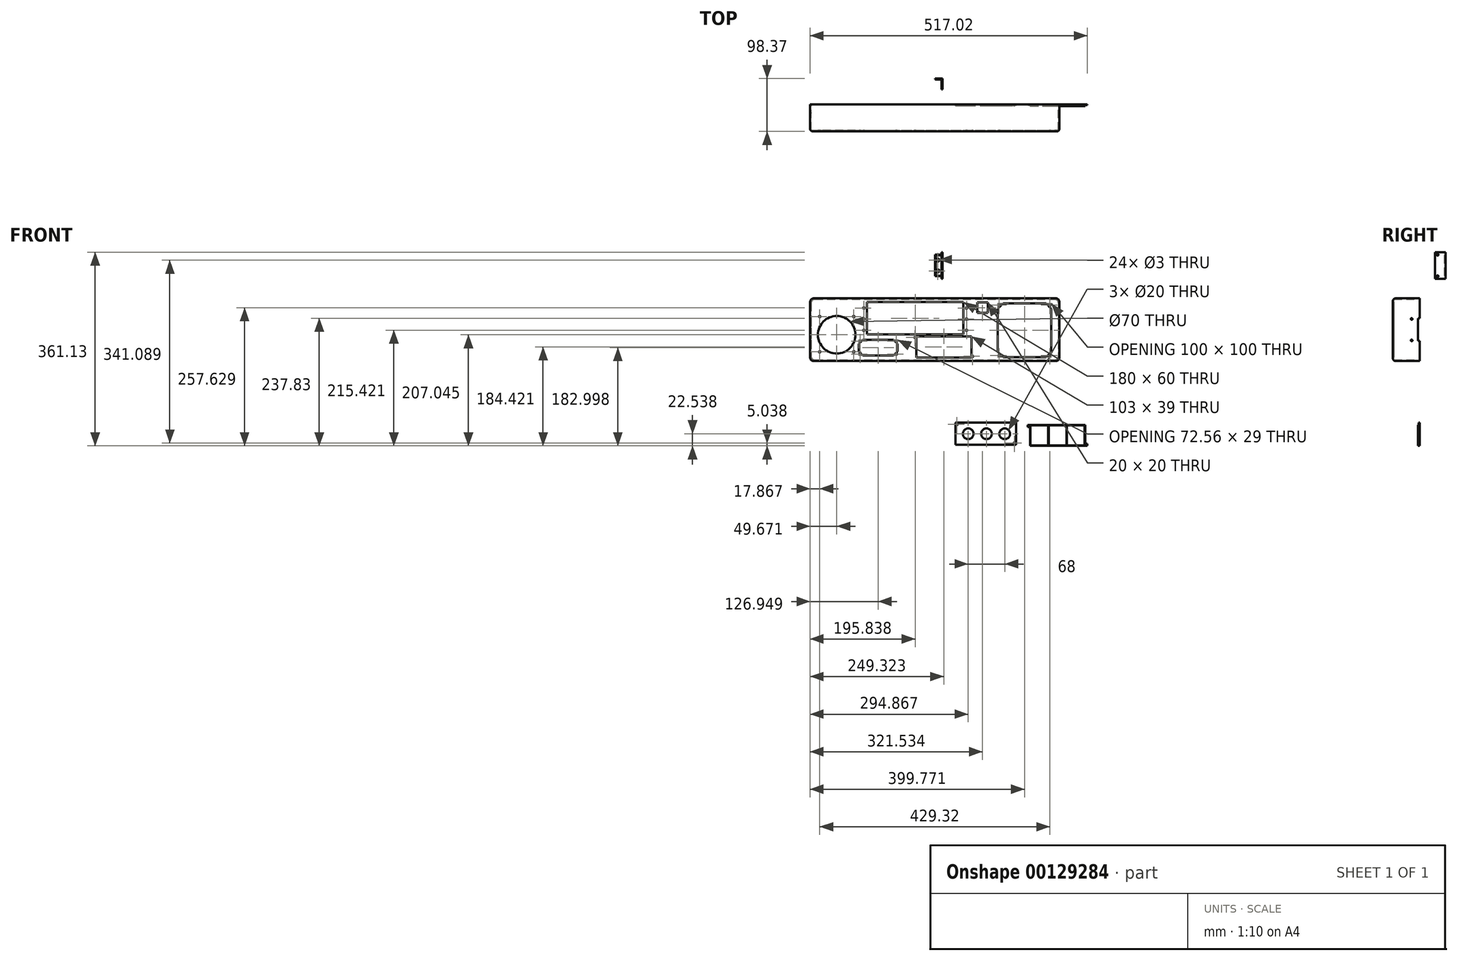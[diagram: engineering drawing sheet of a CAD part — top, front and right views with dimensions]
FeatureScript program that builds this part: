
annotation { "Feature Type Name" : "Feature", "Feature Type Description" : "" }
export const myFeature = defineFeature(function(context is Context, id is Id, definition is map)
    precondition{}
    {
        {
            var Q0;
            Q0=qCreatedBy(makeId("Front.planeOp"),FACE);
            var sketch = newSketch(context, id + "F0", { "sketchPlane" : qUnion([Q0])});
            skLineSegment(sketch, "E0.bottom", {"start": v(-245.15, 85.69) * mm, "end": v(219.85, 85.69) * mm});
            skLineSegment(sketch, "E0.top", {"start": v(-245.15, -31.31) * mm, "end": v(219.85, -31.31) * mm});
            skLineSegment(sketch, "E0.left", {"start": v(-245.15, 85.69) * mm, "end": v(-245.15, -31.31) * mm});
            skLineSegment(sketch, "E0.right", {"start": v(219.85, 85.69) * mm, "end": v(219.85, -31.31) * mm});
            skSolve(sketch);
        }
        {
            var Q0;
            Q0=qSketchRegion(id+"F0",true);
            var Q1;
            Q1=makeQuery(id+"F0.imprint","IMPRINT",FACE,{"disambiguationData":[TD([[makeQuery(id+"F0.imprint","IMPRINT",EDGE,{"derivedFrom":sQuery(id+"F0.wireOp",EDGE,"E0.bottom")}),-1.0]])]});
            extrude(context, id + "F1", {"entities" : qUnion([Q0, Q1]), "depth" : 50 * mm});
        }
        {
            var Q0;
            Q0=makeQuery(id+"F1.opExtrude","CAP_FACE",FACE,{"disambiguationData":[OSD([sQuery(id+"F0.wireOp",EDGE,"E0.bottom"),sQuery(id+"F0.wireOp",EDGE,"E0.top"),sQuery(id+"F0.wireOp",EDGE,"E0.left"),sQuery(id+"F0.wireOp",EDGE,"E0.right")])],"isStart":true});
            shell(context, id + "F2", {"entities" : qUnion([Q0]), "thickness" : 2 * mm});
        }
        {
            var Q0;
            Q0=makeQuery(id+"F1.opExtrude","CAP_FACE",FACE,{"disambiguationData":[OSD([sQuery(id+"F0.wireOp",EDGE,"E0.bottom"),sQuery(id+"F0.wireOp",EDGE,"E0.top"),sQuery(id+"F0.wireOp",EDGE,"E0.left"),sQuery(id+"F0.wireOp",EDGE,"E0.right")])],"isStart":false});
            var sketch = newSketch(context, id + "F3", { "sketchPlane" : qUnion([Q0])});
            skLineSegment(sketch, "E1.bottom", {"start": v(-139.31, 78.52) * mm, "end": v(40.69, 78.52) * mm});
            skLineSegment(sketch, "E1.top", {"start": v(-139.31, 18.52) * mm, "end": v(40.69, 18.52) * mm});
            skLineSegment(sketch, "E1.left", {"start": v(-139.31, 78.52) * mm, "end": v(-139.31, 18.52) * mm});
            skLineSegment(sketch, "E1.right", {"start": v(40.69, 78.52) * mm, "end": v(40.69, 18.52) * mm});
            skLineSegment(sketch, "E2.bottom", {"start": v(66.38, 78.32) * mm, "end": v(86.38, 78.32) * mm});
            skLineSegment(sketch, "E2.top", {"start": v(66.38, 58.32) * mm, "end": v(86.38, 58.32) * mm});
            skLineSegment(sketch, "E2.left", {"start": v(66.38, 78.32) * mm, "end": v(66.38, 58.32) * mm});
            skLineSegment(sketch, "E2.right", {"start": v(86.38, 78.32) * mm, "end": v(86.38, 58.32) * mm});
            skLineSegment(sketch, "E3.bottom", {"start": v(114.52, 76.11) * mm, "end": v(194.72, 76.11) * mm});
            skLineSegment(sketch, "E3.top", {"start": v(114.52, -23.89) * mm, "end": v(194.72, -23.89) * mm});
            skLineSegment(sketch, "E3.left", {"start": v(104.62, 66.21) * mm, "end": v(104.62, -13.99) * mm});
            skLineSegment(sketch, "E3.right", {"start": v(204.62, 66.21) * mm, "end": v(204.62, -13.99) * mm});
            skLineSegment(sketch, "E4.bottom", {"start": v(-128.05, -55.46) * mm, "end": v(-35.05, -55.46) * mm, "construction": true});
            skLineSegment(sketch, "E4.top", {"start": v(-128.05, -91.46) * mm, "end": v(-35.05, -91.46) * mm, "construction": true});
            skLineSegment(sketch, "E4.left", {"start": v(-128.05, -55.46) * mm, "end": v(-128.05, -91.46) * mm, "construction": true});
            skLineSegment(sketch, "E4.right", {"start": v(-35.05, -55.46) * mm, "end": v(-35.05, -91.46) * mm, "construction": true});
            skCircle(sketch, "E5", {"center": v(46.59, 67.55) * mm, "radius": 1.5 * mm});
            skCircle(sketch, "E6", {"center": v(46.59, 47.16) * mm, "radius": 1.5 * mm});
            skCircle(sketch, "E7", {"center": v(46.59, 26.05) * mm, "radius": 1.5 * mm});
            skLineSegment(sketch, "E8.bottom", {"start": v(-233.81, -59.67) * mm, "end": v(-156.81, -59.67) * mm, "construction": true});
            skLineSegment(sketch, "E8.top", {"start": v(-233.81, -136.67) * mm, "end": v(-156.81, -136.67) * mm, "construction": true});
            skLineSegment(sketch, "E8.left", {"start": v(-233.81, -59.67) * mm, "end": v(-233.81, -136.67) * mm, "construction": true});
            skLineSegment(sketch, "E8.right", {"start": v(-156.81, -59.67) * mm, "end": v(-156.81, -136.67) * mm, "construction": true});
            skCircle(sketch, "E9", {"center": v(107.52, 72.86) * mm, "radius": 1.5 * mm});
            skLineSegment(sketch, "E10", {"start": v(104.62, 66.21) * mm, "end": v(114.52, 76.11) * mm});
            skCircle(sketch, "E11", {"center": v(63.6, -74.48) * mm, "radius": 9.5 * mm});
            skLineSegment(sketch, "E12.bottom", {"start": v(46.65, -54.77) * mm, "end": v(139.65, -54.77) * mm});
            skLineSegment(sketch, "E12.top", {"start": v(46.65, -90.77) * mm, "end": v(139.65, -90.77) * mm});
            skLineSegment(sketch, "E12.left", {"start": v(46.65, -54.77) * mm, "end": v(46.65, -90.77) * mm});
            skLineSegment(sketch, "E12.right", {"start": v(139.65, -54.77) * mm, "end": v(139.65, -90.77) * mm});
            skCircle(sketch, "E13", {"center": v(93.62, -74.48) * mm, "radius": 9.5 * mm});
            skCircle(sketch, "E14", {"center": v(123.01, -74.48) * mm, "radius": 9.5 * mm});
            skCircle(sketch, "E15", {"center": v(50.65, -58.77) * mm, "radius": 1.5 * mm});
            skCircle(sketch, "E16", {"center": v(135.65, -86.77) * mm, "radius": 1.5 * mm});
            skLineSegment(sketch, "E17.bottom", {"start": v(-146.7, 8.19) * mm, "end": v(-89.7, 8.19) * mm});
            skLineSegment(sketch, "E17.top", {"start": v(-146.7, -20.81) * mm, "end": v(-89.7, -20.81) * mm});
            skLineSegment(sketch, "E17.left", {"start": v(-154.48, 0.4) * mm, "end": v(-154.48, -13.03) * mm});
            skLineSegment(sketch, "E17.right", {"start": v(-81.92, 0.4) * mm, "end": v(-81.92, -13.03) * mm});
            skCircle(sketch, "E18", {"center": v(-151.98, 5.69) * mm, "radius": 1.5 * mm});
            skCircle(sketch, "E19", {"center": v(-151.98, -18.31) * mm, "radius": 1.5 * mm});
            skCircle(sketch, "E20", {"center": v(-84.42, 5.69) * mm, "radius": 1.5 * mm});
            skCircle(sketch, "E21", {"center": v(-84.42, -18.31) * mm, "radius": 1.5 * mm});
            skLineSegment(sketch, "E22", {"start": v(104.62, -13.99) * mm, "end": v(114.52, -23.89) * mm});
            skLineSegment(sketch, "E23", {"start": v(194.72, -23.89) * mm, "end": v(204.62, -13.99) * mm});
            skLineSegment(sketch, "E24", {"start": v(194.72, 76.11) * mm, "end": v(204.62, 66.21) * mm});
            skCircle(sketch, "E25", {"center": v(107.52, -20.85) * mm, "radius": 1.5 * mm});
            skCircle(sketch, "E26", {"center": v(202.04, -20.85) * mm, "radius": 1.5 * mm});
            skCircle(sketch, "E27", {"center": v(202.04, 72.86) * mm, "radius": 1.5 * mm});
            skCircle(sketch, "E28", {"center": v(-195.48, 17.73) * mm, "radius": 35 * mm});
            skLineSegment(sketch, "E29", {"start": v(-154.48, 0.4) * mm, "end": v(-146.7, 8.19) * mm});
            skLineSegment(sketch, "E30", {"start": v(-89.7, 8.19) * mm, "end": v(-81.92, 0.4) * mm});
            skLineSegment(sketch, "E31", {"start": v(-81.92, -13.03) * mm, "end": v(-89.7, -20.81) * mm});
            skLineSegment(sketch, "E32", {"start": v(-154.48, -13.03) * mm, "end": v(-146.7, -20.81) * mm});
            skCircle(sketch, "E33", {"center": v(-144.85, 67.55) * mm, "radius": 1.5 * mm});
            skCircle(sketch, "E34", {"center": v(-144.85, 47.16) * mm, "radius": 1.5 * mm});
            skCircle(sketch, "E35", {"center": v(-144.85, 26.05) * mm, "radius": 1.5 * mm});
            skCircle(sketch, "E36", {"center": v(-227.28, 51.66) * mm, "radius": 1.5 * mm});
            skCircle(sketch, "E37", {"center": v(-227.28, -14.1) * mm, "radius": 1.5 * mm});
            skCircle(sketch, "E38", {"center": v(-163.64, -14.1) * mm, "radius": 1.5 * mm});
            skLineSegment(sketch, "E39.bottom", {"start": v(-52.33, 15.61) * mm, "end": v(60.67, 15.61) * mm, "construction": true});
            skLineSegment(sketch, "E39.top", {"start": v(-52.33, -25.39) * mm, "end": v(60.67, -25.39) * mm, "construction": true});
            skLineSegment(sketch, "E39.left", {"start": v(-52.33, 15.61) * mm, "end": v(-52.33, -25.39) * mm, "construction": true});
            skLineSegment(sketch, "E39.right", {"start": v(60.67, 15.61) * mm, "end": v(60.67, -25.39) * mm, "construction": true});
            skCircle(sketch, "E40", {"center": v(-163.68, 51.66) * mm, "radius": 1.5 * mm});
            skCircle(sketch, "E41", {"center": v(-49.33, 12.61) * mm, "radius": 1.5 * mm});
            skCircle(sketch, "E42", {"center": v(57.67, -22.39) * mm, "radius": 1.5 * mm});
            skLineSegment(sketch, "E43.bottom", {"start": v(-47.33, 14.61) * mm, "end": v(55.67, 14.61) * mm});
            skLineSegment(sketch, "E43.top", {"start": v(-47.33, -24.39) * mm, "end": v(55.67, -24.39) * mm});
            skLineSegment(sketch, "E43.left", {"start": v(-47.33, 14.61) * mm, "end": v(-47.33, -24.39) * mm});
            skLineSegment(sketch, "E43.right", {"start": v(55.67, 14.61) * mm, "end": v(55.67, -24.39) * mm});
            skLineSegment(sketch, "E44", {"start": v(-230.37, -45.58) * mm, "end": v(-80.37, -45.58) * mm, "construction": true});
            skLineSegment(sketch, "E45", {"start": v(-255.4, -26.53) * mm, "end": v(-255.4, 68.47) * mm, "construction": true});
            skLineSegment(sketch, "E46", {"start": v(-239.28, 22.84) * mm, "end": v(-239.28, -34.99) * mm, "construction": true});
            skSolve(sketch);
        }
        {
            var Q0;
            Q0=makeQuery(id+"F1.opExtrude","SWEPT_EDGE",EDGE,{"disambiguationData":[OSD([sQuery(id+"F0.wireOp",EDGE,"E0.bottom"),sQuery(id+"F0.wireOp",EDGE,"E0.left")])]});
            var Q1;
            Q1=makeQuery(id+"F1.opExtrude","SWEPT_EDGE",EDGE,{"disambiguationData":[OSD([sQuery(id+"F0.wireOp",EDGE,"E0.bottom"),sQuery(id+"F0.wireOp",EDGE,"E0.right")])]});
            var Q2;
            Q2=makeQuery(id+"F1.opExtrude","SWEPT_EDGE",EDGE,{"disambiguationData":[OSD([sQuery(id+"F0.wireOp",EDGE,"E0.top"),sQuery(id+"F0.wireOp",EDGE,"E0.right")])]});
            var Q3;
            Q3=makeQuery(id+"F1.opExtrude","SWEPT_EDGE",EDGE,{"disambiguationData":[OSD([sQuery(id+"F0.wireOp",EDGE,"E0.top"),sQuery(id+"F0.wireOp",EDGE,"E0.left")])]});
            var Q4;
            Q4=makeQuery(id+"F2.opShell","OFFSET_EDGE",EDGE,{"disambiguationData":[OSD([sQuery(id+"F0.wireOp",EDGE,"E0.bottom"),sQuery(id+"F0.wireOp",EDGE,"E0.left")])]});
            var Q5;
            Q5=makeQuery(id+"F2.opShell","OFFSET_EDGE",EDGE,{"disambiguationData":[OSD([sQuery(id+"F0.wireOp",EDGE,"E0.top"),sQuery(id+"F0.wireOp",EDGE,"E0.left")])]});
            var Q6;
            Q6=makeQuery(id+"F2.opShell","OFFSET_EDGE",EDGE,{"disambiguationData":[OSD([sQuery(id+"F0.wireOp",EDGE,"E0.top"),sQuery(id+"F0.wireOp",EDGE,"E0.right")])]});
            var Q7;
            Q7=makeQuery(id+"F2.opShell","OFFSET_EDGE",EDGE,{"disambiguationData":[OSD([sQuery(id+"F0.wireOp",EDGE,"E0.bottom"),sQuery(id+"F0.wireOp",EDGE,"E0.right")])]});
            fillet(context, id + "F4", {"entities" : qUnion([Q0, Q1, Q2, Q3, Q4, Q5, Q6, Q7]), "radius" : 7 * mm, "tangentPropagation" : true, "allowEdgeOverflow" : false});
        }
        {
            var Q0;
            Q0=qSketchRegion(id+"F3",true);
            extrude(context, id + "F5", {"entities" : qUnion([Q0]), "operationType" : NewBodyOperationType.REMOVE, "oppositeDirection" : true, "depth" : 25 * mm});
        }
        {
            var Q0;
            {var subQ0=sQuery(id+"F0.wireOp",EDGE,"E0.right");var subQ1=sQuery(id+"F0.wireOp",EDGE,"E0.bottom");Q0=makeQuery(id+"F4.opFillet","BLEND_EDGE",EDGE,{"blendedFrom":[makeQuery(id+"F1.opExtrude","SWEPT_EDGE",EDGE,{"disambiguationData":[OSD([subQ1,subQ0])]}),makeQuery(id+"F1.opExtrude","CAP_FACE",FACE,{"disambiguationData":[OSD([subQ1,sQuery(id+"F0.wireOp",EDGE,"E0.top"),sQuery(id+"F0.wireOp",EDGE,"E0.left"),subQ0])],"isStart":false})],"blendedInto":[makeQuery(id+"F1.opExtrude","CAP_FACE",FACE,{"disambiguationData":[OSD([subQ1,sQuery(id+"F0.wireOp",EDGE,"E0.top"),sQuery(id+"F0.wireOp",EDGE,"E0.left"),subQ0])],"isStart":false})]});}
            fillet(context, id + "F6", {"entities" : qUnion([Q0]), "radius" : 5 * mm, "tangentPropagation" : true, "allowEdgeOverflow" : false});
        }
        {
            var Q0;
            Q0=makeQuery(id+"F1.opExtrude","CAP_FACE",FACE,{"disambiguationData":[OSD([sQuery(id+"F0.wireOp",EDGE,"E0.bottom"),sQuery(id+"F0.wireOp",EDGE,"E0.top"),sQuery(id+"F0.wireOp",EDGE,"E0.left"),sQuery(id+"F0.wireOp",EDGE,"E0.right")])],"isStart":false});
            var sketch = newSketch(context, id + "F7", { "sketchPlane" : qUnion([Q0])});
            skLineSegment(sketch, "E47.bottom", {"start": v(216.55, -24.6) * mm, "end": v(89.55, -24.6) * mm});
            skLineSegment(sketch, "E47.top", {"start": v(216.55, 75.4) * mm, "end": v(89.55, 75.4) * mm});
            skLineSegment(sketch, "E47.left", {"start": v(216.55, -24.6) * mm, "end": v(216.55, 75.4) * mm});
            skLineSegment(sketch, "E47.right", {"start": v(89.55, -24.6) * mm, "end": v(89.55, 75.4) * mm});
            skLineSegment(sketch, "E48.bottom", {"start": v(-397.12, -53.44) * mm, "end": v(-332.84, -53.44) * mm});
            skLineSegment(sketch, "E48.top", {"start": v(-397.12, -159.24) * mm, "end": v(-332.84, -159.24) * mm});
            skLineSegment(sketch, "E48.left", {"start": v(-397.12, -53.44) * mm, "end": v(-397.12, -159.24) * mm});
            skLineSegment(sketch, "E48.right", {"start": v(-332.84, -53.44) * mm, "end": v(-332.84, -159.24) * mm});
            skLineSegment(sketch, "E49.bottom", {"start": v(38.72, -106.98) * mm, "end": v(60.72, -106.98) * mm, "construction": true});
            skLineSegment(sketch, "E49.top", {"start": v(38.72, -136.98) * mm, "end": v(60.72, -136.98) * mm, "construction": true});
            skLineSegment(sketch, "E49.left", {"start": v(38.72, -106.98) * mm, "end": v(38.72, -136.98) * mm, "construction": true});
            skLineSegment(sketch, "E49.right", {"start": v(60.72, -106.98) * mm, "end": v(60.72, -136.98) * mm, "construction": true});
            skLineSegment(sketch, "E50.bottom", {"start": v(-225.19, 80.69) * mm, "end": v(-165.19, 80.69) * mm});
            skLineSegment(sketch, "E50.top", {"start": v(-225.19, -26.31) * mm, "end": v(-165.19, -26.31) * mm});
            skLineSegment(sketch, "E50.left", {"start": v(-225.19, 80.69) * mm, "end": v(-225.19, -26.31) * mm});
            skLineSegment(sketch, "E50.right", {"start": v(-165.19, 80.69) * mm, "end": v(-165.19, -26.31) * mm});
            skLineSegment(sketch, "E51.bottom", {"start": v(31.72, -103.48) * mm, "end": v(64.72, -103.48) * mm, "construction": true});
            skLineSegment(sketch, "E51.top", {"start": v(31.72, -140.48) * mm, "end": v(64.72, -140.48) * mm, "construction": true});
            skLineSegment(sketch, "E51.left", {"start": v(31.72, -103.48) * mm, "end": v(31.72, -140.48) * mm, "construction": true});
            skLineSegment(sketch, "E51.right", {"start": v(64.72, -103.48) * mm, "end": v(64.72, -140.48) * mm, "construction": true});
            skLineSegment(sketch, "E52.bottom", {"start": v(72.72, -106.98) * mm, "end": v(94.72, -106.98) * mm, "construction": true});
            skLineSegment(sketch, "E52.top", {"start": v(72.72, -136.98) * mm, "end": v(94.72, -136.98) * mm, "construction": true});
            skLineSegment(sketch, "E52.left", {"start": v(72.72, -106.98) * mm, "end": v(72.72, -136.98) * mm, "construction": true});
            skLineSegment(sketch, "E52.right", {"start": v(94.72, -106.98) * mm, "end": v(94.72, -136.98) * mm, "construction": true});
            skLineSegment(sketch, "E53.bottom", {"start": v(65.72, -103.48) * mm, "end": v(98.72, -103.48) * mm, "construction": true});
            skLineSegment(sketch, "E53.top", {"start": v(65.72, -140.48) * mm, "end": v(98.72, -140.48) * mm, "construction": true});
            skLineSegment(sketch, "E53.left", {"start": v(65.72, -103.48) * mm, "end": v(65.72, -140.48) * mm, "construction": true});
            skLineSegment(sketch, "E53.right", {"start": v(98.72, -103.48) * mm, "end": v(98.72, -140.48) * mm, "construction": true});
            skLineSegment(sketch, "E54.bottom", {"start": v(106.72, -106.98) * mm, "end": v(128.72, -106.98) * mm, "construction": true});
            skLineSegment(sketch, "E54.top", {"start": v(106.72, -136.98) * mm, "end": v(128.72, -136.98) * mm, "construction": true});
            skLineSegment(sketch, "E54.left", {"start": v(106.72, -106.98) * mm, "end": v(106.72, -136.98) * mm, "construction": true});
            skLineSegment(sketch, "E54.right", {"start": v(128.72, -106.98) * mm, "end": v(128.72, -136.98) * mm, "construction": true});
            skLineSegment(sketch, "E55.bottom", {"start": v(99.72, -103.48) * mm, "end": v(132.72, -103.48) * mm, "construction": true});
            skLineSegment(sketch, "E55.top", {"start": v(99.72, -140.48) * mm, "end": v(132.72, -140.48) * mm, "construction": true});
            skLineSegment(sketch, "E55.left", {"start": v(99.72, -103.48) * mm, "end": v(99.72, -140.48) * mm, "construction": true});
            skLineSegment(sketch, "E55.right", {"start": v(132.72, -103.48) * mm, "end": v(132.72, -140.48) * mm, "construction": true});
            skCircle(sketch, "E56", {"center": v(83.72, -121.98) * mm, "radius": 10 * mm});
            skCircle(sketch, "E57", {"center": v(49.72, -121.98) * mm, "radius": 10 * mm});
            skCircle(sketch, "E58", {"center": v(117.72, -121.98) * mm, "radius": 10 * mm});
            skSolve(sketch);
        }
        {
            var Q0;
            Q0=makeQuery(id+"F1.opExtrude","SWEPT_FACE",FACE,{"disambiguationData":[OSD([sQuery(id+"F0.wireOp",EDGE,"E0.left")])]});
            var sketch = newSketch(context, id + "F8", { "sketchPlane" : qUnion([Q0])});
            skCircle(sketch, "E59", {"center": v(15, 47.19) * mm, "radius": 1.5 * mm});
            skCircle(sketch, "E60", {"center": v(15, 7.19) * mm, "radius": 1.5 * mm});
            skLineSegment(sketch, "E61", {"start": v(-16.01, 27.19) * mm, "end": v(37.35, 27.19) * mm, "construction": true});
            skPoint(sketch, "E62.middle.positionSnap0", {"position": v(0, 27.19) * mm});
            skPoint(sketch, "E62.centerSnap0", {"position": v(0, 27.19) * mm});
            skLineSegment(sketch, "E63.bottom", {"start": v(3, 6.19) * mm, "end": v(0, 6.19) * mm});
            skLineSegment(sketch, "E63.top", {"start": v(3, 48.19) * mm, "end": v(0, 48.19) * mm});
            skLineSegment(sketch, "E63.left", {"start": v(3, 6.19) * mm, "end": v(3, 48.19) * mm});
            skLineSegment(sketch, "E63.right", {"start": v(0, 6.19) * mm, "end": v(0, 48.19) * mm});
            skPoint(sketch, "E63.middle", {"position": v(1.5, 27.19) * mm});
            skSolve(sketch);
        }
        {
            var Q0;
            Q0=qSketchRegion(id+"F8",true);
            extrude(context, id + "F9", {"entities" : qUnion([Q0]), "operationType" : NewBodyOperationType.REMOVE, "oppositeDirection" : true, "depth" : 500 * mm});
        }
        {
            var Q0;
            Q0=qCreatedBy(makeId("Right.planeOp"),FACE);
            var sketch = newSketch(context, id + "F10", { "sketchPlane" : qUnion([Q0])});
            skLineSegment(sketch, "E64.bottom", {"start": v(28.37, 121.82) * mm, "end": v(48.37, 121.82) * mm});
            skLineSegment(sketch, "E64.top", {"start": v(28.37, 171.82) * mm, "end": v(48.37, 171.82) * mm});
            skLineSegment(sketch, "E64.left", {"start": v(28.37, 121.82) * mm, "end": v(28.37, 171.82) * mm});
            skLineSegment(sketch, "E64.right", {"start": v(48.37, 121.82) * mm, "end": v(48.37, 171.82) * mm});
            skPoint(sketch, "E64.middle", {"position": v(38.37, 146.82) * mm});
            skCircle(sketch, "E65", {"center": v(33.37, 166.82) * mm, "radius": 1.5 * mm});
            skCircle(sketch, "E66", {"center": v(33.37, 126.82) * mm, "radius": 1.5 * mm});
            skSolve(sketch);
        }
        {
            var Q0;
            Q0=qSketchRegion(id+"F10",true);
            extrude(context, id + "F11", {"entities" : qUnion([Q0]), "depth" : 2 * mm});
        }
        {
            var Q0;
            Q0=makeQuery(id+"F11.opExtrude","SWEPT_FACE",FACE,{"disambiguationData":[OSD([sQuery(id+"F10.wireOp",EDGE,"E64.right")])]});
            var sketch = newSketch(context, id + "F12", { "sketchPlane" : qUnion([Q0])});
            skLineSegment(sketch, "E67.bottom", {"start": v(0, 166.82) * mm, "end": v(12, 166.82) * mm});
            skLineSegment(sketch, "E67.top", {"start": v(0, 126.82) * mm, "end": v(12, 126.82) * mm});
            skLineSegment(sketch, "E67.left", {"start": v(0, 166.82) * mm, "end": v(0, 126.82) * mm});
            skLineSegment(sketch, "E67.right", {"start": v(12, 166.82) * mm, "end": v(12, 126.82) * mm});
            skSolve(sketch);
        }
        {
            var Q0;
            Q0=qSketchRegion(id+"F12",true);
            extrude(context, id + "F13", {"entities" : qUnion([Q0]), "operationType" : NewBodyOperationType.ADD, "oppositeDirection" : true, "depth" : 2 * mm});
        }
        {
            var Q0;
            Q0=makeQuery(id+"F13.opExtrude","CAP_FACE",FACE,{"disambiguationData":[OSD([sQuery(id+"F12.wireOp",EDGE,"E67.bottom"),sQuery(id+"F12.wireOp",EDGE,"E67.top"),sQuery(id+"F12.wireOp",EDGE,"E67.left"),sQuery(id+"F12.wireOp",EDGE,"E67.right")])],"isStart":false});
            var sketch = newSketch(context, id + "F14", { "sketchPlane" : qUnion([Q0])});
            skCircle(sketch, "E68", {"center": v(-7, 156.82) * mm, "radius": 1.5 * mm});
            skCircle(sketch, "E69", {"center": v(-7, 136.82) * mm, "radius": 1.5 * mm});
            skSolve(sketch);
        }
        {
            var Q0;
            Q0=sQuery(id+"F14.wireOp",VERTEX,"E68.center");
            var Q1;
            Q1=sQuery(id+"F14.wireOp",VERTEX,"E69.center");
            var Q2;
            Q2=makeQuery(id+"F11.opExtrude","SWEPT_BODY",BODY,{"disambiguationData":[OSD([sQuery(id+"F10.wireOp",EDGE,"E64.bottom"),sQuery(id+"F10.wireOp",EDGE,"E64.top"),sQuery(id+"F10.wireOp",EDGE,"E64.left"),sQuery(id+"F10.wireOp",EDGE,"E64.right"),sQuery(id+"F10.wireOp",EDGE,"E65"),sQuery(id+"F10.wireOp",EDGE,"E66")])]});
            hole(context, id + "F15", {"style" : HoleStyle.C_SINK, "endStyle" : HoleEndStyle.THROUGH, "holeDiameter" : 3 * mm, "cSinkDiameter" : 5.7 * mm, "cSinkAngle" : 90 * degree, "locations" : qUnion([Q0, Q1]), "scope" : qUnion([Q2]), "isTappedThrough" : true});
        }
        {
            var Q0;
            Q0=makeQuery(id+"F13.opExtrude","CAP_EDGE",EDGE,{"disambiguationData":[OSD([sQuery(id+"F12.wireOp",EDGE,"E67.bottom")])],"isStart":false});
            var Q1;
            Q1=makeQuery(id+"F13.opExtrude","CAP_EDGE",EDGE,{"disambiguationData":[OSD([sQuery(id+"F12.wireOp",EDGE,"E67.right")])],"isStart":false});
            var Q2;
            Q2=makeQuery(id+"F13.opExtrude","CAP_EDGE",EDGE,{"disambiguationData":[OSD([sQuery(id+"F12.wireOp",EDGE,"E67.top")])],"isStart":false});
            chamfer(context, id + "F16", {"entities" : qUnion([Q0, Q1, Q2]), "width" : 1 * mm, "tangentPropagation" : true});
        }
        {
            var Q0;
            Q0=qCreatedBy(makeId("Front.planeOp"),FACE);
            var sketch = newSketch(context, id + "F17", { "sketchPlane" : qUnion([Q0])});
            skCircle(sketch, "E70", {"center": v(49.72, -166.77) * mm, "radius": 10 * mm});
            skCircle(sketch, "E71", {"center": v(83.72, -166.77) * mm, "radius": 10 * mm});
            skCircle(sketch, "E72", {"center": v(117.72, -166.77) * mm, "radius": 10 * mm});
            skCircle(sketch, "E73", {"center": v(28.72, -149.27) * mm, "radius": 1.5 * mm});
            skCircle(sketch, "E74", {"center": v(135.72, -184.27) * mm, "radius": 1.5 * mm});
            skLineSegment(sketch, "E75.bottom", {"start": v(25.72, -146.27) * mm, "end": v(138.72, -146.27) * mm});
            skLineSegment(sketch, "E75.top", {"start": v(25.72, -187.27) * mm, "end": v(138.72, -187.27) * mm});
            skLineSegment(sketch, "E75.left", {"start": v(25.72, -146.27) * mm, "end": v(25.72, -187.27) * mm});
            skLineSegment(sketch, "E75.right", {"start": v(138.72, -146.27) * mm, "end": v(138.72, -187.27) * mm});
            skSolve(sketch);
        }
        {
            var Q0;
            Q0=makeQuery(id+"F17.imprint","IMPRINT",FACE,{"disambiguationData":[TD([[makeQuery(id+"F17.imprint","IMPRINT",EDGE,{"derivedFrom":sQuery(id+"F17.wireOp",EDGE,"E70")}),-1.0]])]});
            extrude(context, id + "F18", {"entities" : qUnion([Q0]), "depth" : 2 * mm});
        }
        {
            var Q0;
            Q0=qCreatedBy(makeId("Front.planeOp"),FACE);
            var sketch = newSketch(context, id + "F19", { "sketchPlane" : qUnion([Q0])});
            skLineSegment(sketch, "E76.bottom", {"start": v(164.87, -150.31) * mm, "end": v(267.87, -150.31) * mm});
            skLineSegment(sketch, "E76.top", {"start": v(164.87, -189.31) * mm, "end": v(267.87, -189.31) * mm});
            skLineSegment(sketch, "E76.left", {"start": v(164.87, -150.31) * mm, "end": v(164.87, -189.31) * mm});
            skLineSegment(sketch, "E76.right", {"start": v(267.87, -150.31) * mm, "end": v(267.87, -189.31) * mm});
            skLineSegment(sketch, "E77.bottom", {"start": v(164.87, -150.31) * mm, "end": v(160.87, -150.31) * mm});
            skLineSegment(sketch, "E77.top", {"start": v(164.87, -154.31) * mm, "end": v(160.87, -154.31) * mm});
            skLineSegment(sketch, "E77.left", {"start": v(164.87, -150.31) * mm, "end": v(164.87, -154.31) * mm});
            skLineSegment(sketch, "E77.right", {"start": v(160.87, -150.31) * mm, "end": v(160.87, -154.31) * mm});
            skLineSegment(sketch, "E78.bottom", {"start": v(267.87, -189.31) * mm, "end": v(271.87, -189.31) * mm});
            skLineSegment(sketch, "E78.top", {"start": v(267.87, -185.31) * mm, "end": v(271.87, -185.31) * mm});
            skLineSegment(sketch, "E78.left", {"start": v(267.87, -189.31) * mm, "end": v(267.87, -185.31) * mm});
            skLineSegment(sketch, "E78.right", {"start": v(271.87, -189.31) * mm, "end": v(271.87, -185.31) * mm});
            skCircle(sketch, "E79", {"center": v(162.87, -152.31) * mm, "radius": 1.5 * mm});
            skCircle(sketch, "E80", {"center": v(269.87, -187.31) * mm, "radius": 1.5 * mm});
            skSolve(sketch);
        }
        {
            var Q0;
            Q0=makeQuery(id+"F19.imprint","IMPRINT",FACE,{"disambiguationData":[TD([[makeQuery(id+"F19.imprint","IMPRINT",EDGE,{"derivedFrom":sQuery(id+"F19.wireOp",EDGE,"E76.bottom")}),-1.0]])]});
            extrude(context, id + "F20", {"entities" : qUnion([Q0]), "depth" : 3 * mm});
        }
        {
            var Q0;
            Q0=makeQuery(id+"F19.imprint","IMPRINT",FACE,{"disambiguationData":[TD([[makeQuery(id+"F19.imprint","IMPRINT",EDGE,{"derivedFrom":sQuery(id+"F19.wireOp",EDGE,"E77.bottom")}),1.0]])]});
            var Q1;
            Q1=makeQuery(id+"F19.imprint","IMPRINT",FACE,{"disambiguationData":[TD([[makeQuery(id+"F19.imprint","IMPRINT",EDGE,{"derivedFrom":sQuery(id+"F19.wireOp",EDGE,"E78.bottom")}),1.0]])]});
            extrude(context, id + "F21", {"entities" : qUnion([Q0, Q1]), "operationType" : NewBodyOperationType.ADD, "depth" : 1 * mm});
        }
        {
            var Q0;
            Q0=makeQuery(id+"F20.opExtrude","CAP_FACE",FACE,{"disambiguationData":[OSD([sQuery(id+"F19.wireOp",EDGE,"E76.bottom"),sQuery(id+"F19.wireOp",EDGE,"E76.top"),sQuery(id+"F19.wireOp",EDGE,"E76.left"),sQuery(id+"F19.wireOp",EDGE,"E76.right"),sQuery(id+"F19.wireOp",EDGE,"E77.left"),sQuery(id+"F19.wireOp",EDGE,"E78.left")])],"isStart":false});
            var sketch = newSketch(context, id + "F22", { "sketchPlane" : qUnion([Q0])});
            skLineSegment(sketch, "E81.bottom", {"start": v(165.87, -151.31) * mm, "end": v(198.87, -151.31) * mm});
            skLineSegment(sketch, "E81.top", {"start": v(165.87, -188.31) * mm, "end": v(198.87, -188.31) * mm});
            skLineSegment(sketch, "E81.left", {"start": v(165.87, -151.31) * mm, "end": v(165.87, -188.31) * mm});
            skLineSegment(sketch, "E81.right", {"start": v(198.87, -151.31) * mm, "end": v(198.87, -188.31) * mm});
            skLineSegment(sketch, "E82.bottom", {"start": v(199.87, -151.31) * mm, "end": v(232.87, -151.31) * mm});
            skLineSegment(sketch, "E82.top", {"start": v(199.87, -188.31) * mm, "end": v(232.87, -188.31) * mm});
            skLineSegment(sketch, "E82.left", {"start": v(199.87, -151.31) * mm, "end": v(199.87, -188.31) * mm});
            skLineSegment(sketch, "E82.right", {"start": v(232.87, -151.31) * mm, "end": v(232.87, -188.31) * mm});
            skLineSegment(sketch, "E83.bottom", {"start": v(233.87, -151.31) * mm, "end": v(266.87, -151.31) * mm});
            skLineSegment(sketch, "E83.top", {"start": v(233.87, -188.31) * mm, "end": v(266.87, -188.31) * mm});
            skLineSegment(sketch, "E83.left", {"start": v(233.87, -151.31) * mm, "end": v(233.87, -188.31) * mm});
            skLineSegment(sketch, "E83.right", {"start": v(266.87, -151.31) * mm, "end": v(266.87, -188.31) * mm});
            skLineSegment(sketch, "E84.bottom", {"start": v(198.87, -161.31) * mm, "end": v(199.87, -161.31) * mm});
            skLineSegment(sketch, "E84.top", {"start": v(198.87, -178.31) * mm, "end": v(199.87, -178.31) * mm});
            skLineSegment(sketch, "E84.left", {"start": v(198.87, -161.31) * mm, "end": v(198.87, -178.31) * mm});
            skLineSegment(sketch, "E84.right", {"start": v(199.87, -161.31) * mm, "end": v(199.87, -178.31) * mm});
            skLineSegment(sketch, "E85.bottom", {"start": v(232.87, -161.31) * mm, "end": v(233.87, -161.31) * mm});
            skLineSegment(sketch, "E85.top", {"start": v(232.87, -178.31) * mm, "end": v(233.87, -178.31) * mm});
            skLineSegment(sketch, "E85.left", {"start": v(232.87, -161.31) * mm, "end": v(232.87, -178.31) * mm});
            skLineSegment(sketch, "E85.right", {"start": v(233.87, -161.31) * mm, "end": v(233.87, -178.31) * mm});
            skSolve(sketch);
        }
        {
            var Q0;
            {var subQ1=sQuery(id+"F22.wireOp",EDGE,"E81.bottom");Q0=makeQuery(id+"F22.imprint","IMPRINT",FACE,{"disambiguationData":[TD([[makeQuery(id+"F22.imprint","IMPRINT",EDGE,{"derivedFrom":subQ1}),-1.0]])]});}
            var Q1;
            {var subQ3=sQuery(id+"F22.wireOp",EDGE,"E82.bottom");Q1=makeQuery(id+"F22.imprint","IMPRINT",FACE,{"disambiguationData":[TD([[makeQuery(id+"F22.imprint","IMPRINT",EDGE,{"derivedFrom":subQ3}),-1.0]])]});}
            var Q2;
            {var subQ1=sQuery(id+"F22.wireOp",EDGE,"E83.bottom");Q2=makeQuery(id+"F22.imprint","IMPRINT",FACE,{"disambiguationData":[TD([[makeQuery(id+"F22.imprint","IMPRINT",EDGE,{"derivedFrom":subQ1}),-1.0]])]});}
            extrude(context, id + "F23", {"entities" : qUnion([Q0, Q1, Q2]), "operationType" : NewBodyOperationType.REMOVE, "oppositeDirection" : true, "depth" : 2 * mm});
        }
        {
            var Q0;
            Q0=makeQuery(id+"F22.imprint","IMPRINT",FACE,{"disambiguationData":[TD([[makeQuery(id+"F22.imprint","IMPRINT",EDGE,{"derivedFrom":sQuery(id+"F22.wireOp",EDGE,"E84.bottom")}),-1.0]])]});
            var Q1;
            Q1=makeQuery(id+"F22.imprint","IMPRINT",FACE,{"disambiguationData":[TD([[makeQuery(id+"F22.imprint","IMPRINT",EDGE,{"derivedFrom":sQuery(id+"F22.wireOp",EDGE,"E85.bottom")}),-1.0]])]});
            extrude(context, id + "F24", {"entities" : qUnion([Q0, Q1]), "operationType" : NewBodyOperationType.REMOVE, "oppositeDirection" : true, "depth" : 3 * mm});
        }
    });
